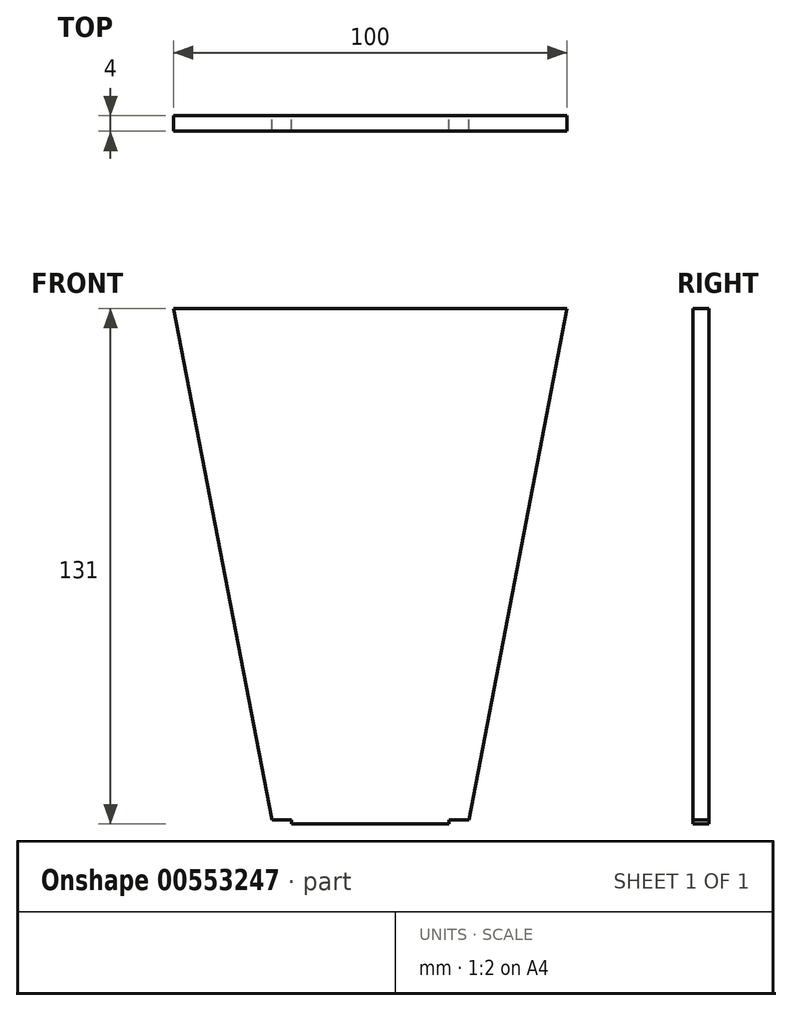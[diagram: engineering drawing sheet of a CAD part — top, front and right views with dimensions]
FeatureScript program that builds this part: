
annotation { "Feature Type Name" : "Feature", "Feature Type Description" : "" }
export const myFeature = defineFeature(function(context is Context, id is Id, definition is map)
    precondition{}
    {
        {
            var Q0;
            Q0=qCreatedBy(makeId("Front.planeOp"),FACE);
            var sketch = newSketch(context, id + "F0", { "sketchPlane" : qUnion([Q0])});
            skLineSegment(sketch, "E0", {"start": v(0, 0) * mm, "end": v(-50, 0) * mm});
            skLineSegment(sketch, "E1", {"start": v(0, 0) * mm, "end": v(50, 0) * mm});
            skLineSegment(sketch, "E2", {"start": v(0, 0) * mm, "end": v(0, -130) * mm});
            skLineSegment(sketch, "E3", {"start": v(0, -130) * mm, "end": v(25, -130) * mm});
            skLineSegment(sketch, "E4", {"start": v(25, -130) * mm, "end": v(-25, -130) * mm});
            skPoint(sketch, "E4.endSnap0", {"position": v(12.5, -130) * mm});
            skLineSegment(sketch, "E5", {"start": v(-25, -130) * mm, "end": v(-50, 0) * mm});
            skLineSegment(sketch, "E6", {"start": v(25, -130) * mm, "end": v(50, 0) * mm});
            skLineSegment(sketch, "E7", {"start": v(0, -130) * mm, "end": v(20, -130) * mm});
            skLineSegment(sketch, "E8", {"start": v(20, -130) * mm, "end": v(-20, -130) * mm});
            skLineSegment(sketch, "E9", {"start": v(-20, -130) * mm, "end": v(-20, -131) * mm});
            skLineSegment(sketch, "E10", {"start": v(-20, -131) * mm, "end": v(20, -131) * mm});
            skLineSegment(sketch, "E11", {"start": v(20, -131) * mm, "end": v(20, -130) * mm});
            skSolve(sketch);
        }
        {
            var Q0;
            Q0 = qSketchRegion(id + "F0", true);
            extrude(context, id + "F1", {"entities" : qUnion([Q0]), "depth" : 4 * mm, "offsetDistance" : 25 * mm});
        }
    });
